# Revit family: Gira_5500000
name_source: partatom
category: Elektroinstallationen
revit_build: Autodesk Revit 2017 (Build: 20160225_1515(x64)
units: mm (PartAtom-declared; Revit-internal decimal feet)

## family parameters
Basisbauteil = Fläche
Beim Laden mit Abzugskörper schneiden = Nein
Bemaßung runder Anschluss = Durchmesser verwenden
Beschriftungsausrichtung beibehalten = Nein
Gemeinsam genutzt = Nein
Raumberechnungspunkt = Nein
Teiletyp = Normal

## types (1)
- TKS-IP-Datenschnittst. Türko
    Anzahl der Eingänge = 0
    BIM = https://media.stage.bim.site X1 REG KNX.rfa
    BIMSITE_PRODUCT_ID = 25b31a60b08b35c61d503afbc6bb24e588bc6163
    Beschreibung = TKS-IP-Datenschnittstelle   Merkmale:  Die Datenschnittstelle dient dazu, die derzeitige Pushbutton-Inbetriebnahme um eine komfortable Inbetriebnahme mittels PC Laptop zu erweitern und den 2-Draht-Bus an IP anzubinden.  Projektierung über Gira Projekt Assistent (GPA).  Inbetriebnahme großer Projekte.  Auslesen der Projektierungsdaten von Bestandsanlagen.  Anbindung Gira 2-Draht-Bus an IP.  Nur für den Gebrauch im Innenbereich geeignet.
    Breite in Teilungseinheiten = 2
    Bussystem Funkbus = Nein
    Bussystem KNX = Nein
    Bussystem KNX-Funk = Nein
    Bussystem LON = Nein
    Bussystem Powernet = Nein
    Datenblatt = https://media.stage.bim.site
    Datenblatt 1 = https://media.stage.bim.site
    Funktion = steuern/regeln
    Funktion Schalten = Nein
    GTIN = 4010337052685
    HAN = 5500000
    HeinzeBIM = https://www.heinze.de
    Hersteller = Gira
    Installationstechnik = 2-Draht
    Kosten = 0 $
    Max. Anzahl der Jalousieausgänge = 0
    Max. Schaltleistung [Voltampere] = 0
    Mit Busankopplung = Nein
    Mit LED-Anzeige = Nein
    Montageart = DIN-Schiene
    Produktseite = https://media.stage.bim.site
    Typname = TKS-IP-Datenschnittst. Türko
    URL = https://www.gira.de
    Vor Ort-/Handbedienung = Nein
    Vorgabe-Ansicht = 1219 mm

## geometry (parser evidence)
native form markers: Sweep x2
no freeform markers — native parametric forms only
